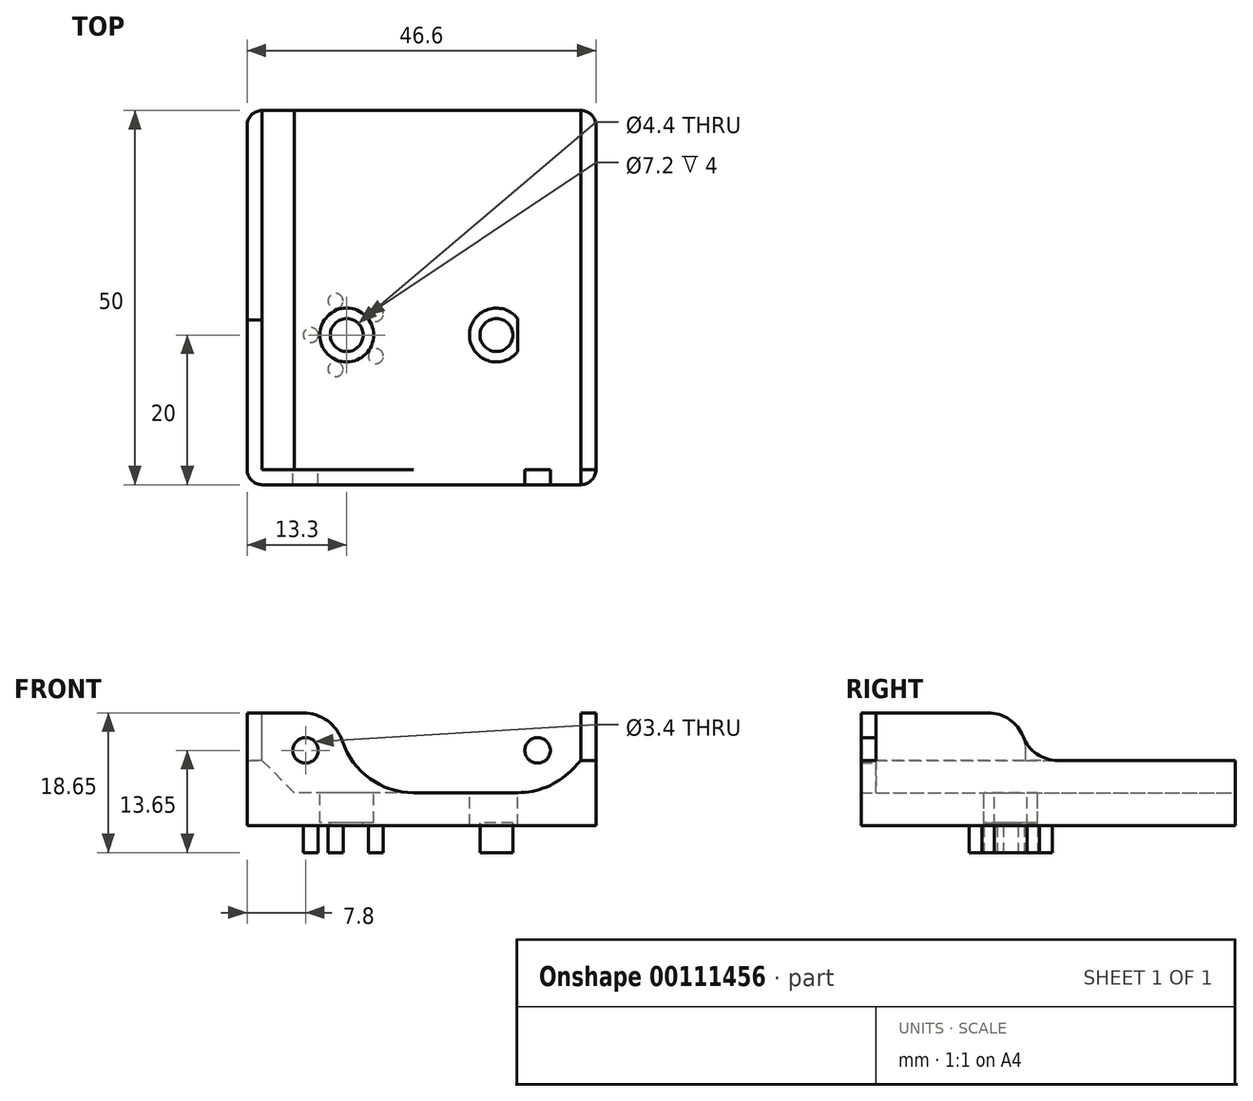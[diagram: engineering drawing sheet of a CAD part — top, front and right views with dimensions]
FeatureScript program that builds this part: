
annotation { "Feature Type Name" : "Feature", "Feature Type Description" : "" }
export const myFeature = defineFeature(function(context is Context, id is Id, definition is map)
    precondition{}
    {
        {
            var Q0;
            Q0=qCreatedBy(makeId("Front.planeOp"),FACE);
            var sketch = newSketch(context, id + "F0", { "sketchPlane" : qUnion([Q0])});
            skLineSegment(sketch, "E0", {"start": v(-23.3, 0) * mm, "end": v(0, 0) * mm});
            skLineSegment(sketch, "E1", {"start": v(0, 8) * mm, "end": v(-17, 8) * mm});
            skLineSegment(sketch, "E2", {"start": v(-17, 8) * mm, "end": v(-21.3, 12.3) * mm});
            skLineSegment(sketch, "E3", {"start": v(0, 0) * mm, "end": v(0, 8) * mm, "construction": true});
            skLineSegment(sketch, "E4", {"start": v(-21.3, 12.3) * mm, "end": v(-23.3, 12.3) * mm});
            skLineSegment(sketch, "E5", {"start": v(-23.3, 12.3) * mm, "end": v(-23.3, 0) * mm});
            skLineSegment(sketch, "E6.MirrorCS", {"start": v(0, 8) * mm, "end": v(17, 8) * mm});
            skLineSegment(sketch, "E7.MirrorCS", {"start": v(17, 8) * mm, "end": v(21.3, 12.3) * mm});
            skLineSegment(sketch, "E8.MirrorCS", {"start": v(21.3, 12.3) * mm, "end": v(23.3, 12.3) * mm});
            skLineSegment(sketch, "E9.MirrorCS", {"start": v(23.3, 12.3) * mm, "end": v(23.3, 0) * mm});
            skLineSegment(sketch, "E10.MirrorCS", {"start": v(23.3, 0) * mm, "end": v(0, 0) * mm});
            skSolve(sketch);
        }
        {
            var Q0;
            Q0=makeQuery(id+"F0.imprint","IMPRINT",FACE,{"disambiguationData":[TD([[makeQuery(id+"F0.imprint","IMPRINT",EDGE,{"derivedFrom":sQuery(id+"F0.wireOp",EDGE,"E0")}),1.0]])]});
            extrude(context, id + "F1", {"entities" : qUnion([Q0]), "endBound" : BoundingType.SYMMETRIC, "depth" : 48 * mm});
        }
        {
            var Q0;
            Q0=makeQuery(id+"F1.opExtrude","CAP_FACE",FACE,{"disambiguationData":[OSD([sQuery(id+"F0.wireOp",EDGE,"E0"),sQuery(id+"F0.wireOp",EDGE,"E1"),sQuery(id+"F0.wireOp",EDGE,"E2"),sQuery(id+"F0.wireOp",EDGE,"E4"),sQuery(id+"F0.wireOp",EDGE,"E5"),sQuery(id+"F0.wireOp",EDGE,"E6.MirrorCS"),sQuery(id+"F0.wireOp",EDGE,"E7.MirrorCS"),sQuery(id+"F0.wireOp",EDGE,"E8.MirrorCS"),sQuery(id+"F0.wireOp",EDGE,"E9.MirrorCS"),sQuery(id+"F0.wireOp",EDGE,"E10.MirrorCS")])],"isStart":false});
            var sketch = newSketch(context, id + "F2", { "sketchPlane" : qUnion([Q0])});
            skLineSegment(sketch, "E11", {"start": v(0, 8) * mm, "end": v(0, 29.15) * mm, "construction": true});
            skCircle(sketch, "E12", {"center": v(-15.5, 13.65) * mm, "radius": 1.7 * mm});
            skCircle(sketch, "E13.MirrorC", {"center": v(15.5, 13.65) * mm, "radius": 1.7 * mm});
            skLineSegment(sketch, "E14", {"start": v(-23.3, 12.3) * mm, "end": v(-23.3, 18.65) * mm});
            skLineSegment(sketch, "E15", {"start": v(-23.3, 18.65) * mm, "end": v(-10.3, 18.65) * mm});
            skLineSegment(sketch, "E16", {"start": v(-10.3, 18.65) * mm, "end": v(-10.3, 8) * mm});
            skLineSegment(sketch, "E17.MirrorCS", {"start": v(23.3, 12.3) * mm, "end": v(23.3, 18.65) * mm});
            skLineSegment(sketch, "E18.MirrorCS", {"start": v(23.3, 18.65) * mm, "end": v(10.3, 18.65) * mm});
            skLineSegment(sketch, "E19.MirrorCS", {"start": v(10.3, 18.65) * mm, "end": v(10.3, 8) * mm});
            skSolve(sketch);
        }
        {
            var Q0;
            Q0=makeQuery(id+"F2.imprint","IMPRINT",FACE,{"disambiguationData":[TD([[makeQuery(id+"F2.imprint","IMPRINT",EDGE,{"derivedFrom":sQuery(id+"F2.wireOp",EDGE,"E12")}),-1.0]])]});
            var Q1;
            Q1=makeQuery(id+"F2.imprint","IMPRINT",FACE,{"disambiguationData":[TD([[makeQuery(id+"F2.imprint","IMPRINT",EDGE,{"derivedFrom":sQuery(id+"F2.wireOp",EDGE,"E13.MirrorC")}),1.0]])]});
            var Q2;
            {var subQ0=makeQuery(id+"F1.opExtrude","CAP_EDGE",EDGE,{"disambiguationData":[OSD([sQuery(id+"F0.wireOp",EDGE,"E2")])],"isStart":false});Q2=makeQuery(id+"F2.imprint","IMPRINT",FACE,{"disambiguationData":[TD([[makeQuery(id+"F2.imprint","IMPRINT",EDGE,{"derivedFrom":subQ0}),1.0]])]});}
            extrude(context, id + "F3", {"entities" : qUnion([Q0, Q1, Q2]), "operationType" : NewBodyOperationType.ADD, "depth" : 2 * mm});
        }
        {
            var Q0;
            Q0=makeQuery(id+"F3.opExtrude","SWEPT_EDGE",EDGE,{"disambiguationData":[OSD([sQuery(id+"F2.wireOp",EDGE,"E15"),sQuery(id+"F2.wireOp",EDGE,"E16")])]});
            var Q1;
            Q1=makeQuery(id+"F3.opExtrude","SWEPT_EDGE",EDGE,{"disambiguationData":[OSD([sQuery(id+"F2.wireOp",EDGE,"E18.MirrorCS"),sQuery(id+"F2.wireOp",EDGE,"E19.MirrorCS")])]});
            fillet(context, id + "F4", {"entities" : qUnion([Q0, Q1]), "radius" : 5.5 * mm, "tangentPropagation" : true, "allowEdgeOverflow" : false});
        }
        {
            var Q0;
            Q0=makeQuery(id+"F3.opExtrude","SWEPT_EDGE",EDGE,{"disambiguationData":[OSD([sQuery(id+"F0.wireOp",EDGE,"E1"),sQuery(id+"F0.wireOp",EDGE,"E6.MirrorCS"),sQuery(id+"F2.wireOp",EDGE,"E16")])]});
            var Q1;
            Q1=makeQuery(id+"F3.opExtrude","SWEPT_EDGE",EDGE,{"disambiguationData":[OSD([sQuery(id+"F0.wireOp",EDGE,"E1"),sQuery(id+"F0.wireOp",EDGE,"E6.MirrorCS"),sQuery(id+"F2.wireOp",EDGE,"E19.MirrorCS")])]});
            fillet(context, id + "F5", {"entities" : qUnion([Q0, Q1]), "radius" : 10 * mm, "tangentPropagation" : true, "allowEdgeOverflow" : false});
        }
        {
            var Q0;
            {var subQ0=sQuery(id+"F2.wireOp",EDGE,"E13.MirrorC");var subQ1=sQuery(id+"F0.wireOp",EDGE,"E9.MirrorCS");var subQ2=sQuery(id+"F0.wireOp",EDGE,"E6.MirrorCS");var subQ3=sQuery(id+"F0.wireOp",EDGE,"E1");var subQ4=sQuery(id+"F2.wireOp",EDGE,"E19.MirrorCS");var subQ5=sQuery(id+"F2.wireOp",EDGE,"E17.MirrorCS");var subQ6=sQuery(id+"F2.wireOp",EDGE,"E18.MirrorCS");Q0=makeQuery(id+"F3.boolean.opBoolean","SPLIT",FACE,{"disambiguationData":[TD([makeQuery(id+"F1.opExtrude","SWEPT_FACE",FACE,{"disambiguationData":[OSD([sQuery(id+"F0.wireOp",EDGE,"E7.MirrorCS")])]})])],"derivedFrom":makeQuery(id+"F3.opExtrude","CAP_FACE",FACE,{"disambiguationData":[OSD([sQuery(id+"F0.wireOp",EDGE,"E0"),subQ3,sQuery(id+"F0.wireOp",EDGE,"E5"),subQ2,subQ1,sQuery(id+"F0.wireOp",EDGE,"E10.MirrorCS"),sQuery(id+"F2.wireOp",EDGE,"E12"),subQ0,sQuery(id+"F2.wireOp",EDGE,"E14"),sQuery(id+"F2.wireOp",EDGE,"E15"),sQuery(id+"F2.wireOp",EDGE,"E16"),subQ5,subQ6,subQ4])],"isStart":true})});}
            var sketch = newSketch(context, id + "F6", { "sketchPlane" : qUnion([Q0])});
            skLineSegment(sketch, "E20.bottom", {"start": v(-21.3, 12.3) * mm, "end": v(-23.3, 12.3) * mm});
            skLineSegment(sketch, "E20.top", {"start": v(-21.3, 18.65) * mm, "end": v(-23.3, 18.65) * mm});
            skLineSegment(sketch, "E20.left", {"start": v(-21.3, 12.3) * mm, "end": v(-21.3, 18.65) * mm});
            skLineSegment(sketch, "E20.right", {"start": v(-23.3, 12.3) * mm, "end": v(-23.3, 18.65) * mm});
            skLineSegment(sketch, "E21", {"start": v(0, 8) * mm, "end": v(0, 18.65) * mm, "construction": true});
            skLineSegment(sketch, "E22.MirrorCS", {"start": v(23.3, 12.3) * mm, "end": v(23.3, 18.65) * mm});
            skLineSegment(sketch, "E23.MirrorCS", {"start": v(21.3, 12.3) * mm, "end": v(21.3, 18.65) * mm});
            skLineSegment(sketch, "E24.MirrorCS", {"start": v(21.3, 18.65) * mm, "end": v(23.3, 18.65) * mm});
            skLineSegment(sketch, "E25.MirrorCS", {"start": v(21.3, 12.3) * mm, "end": v(23.3, 12.3) * mm});
            skSolve(sketch);
        }
        {
            var Q0;
            Q0 = qSketchRegion(id + "F6", true);
            extrude(context, id + "F7", {"entities" : qUnion([Q0]), "operationType" : NewBodyOperationType.ADD, "depth" : 20 * mm});
        }
        {
            var Q0;
            Q0=makeQuery(id+"F7.opExtrude","CAP_EDGE",EDGE,{"disambiguationData":[OSD([sQuery(id+"F6.wireOp",EDGE,"E20.top")])],"isStart":false});
            var Q1;
            Q1=makeQuery(id+"F7.opExtrude","CAP_EDGE",EDGE,{"disambiguationData":[OSD([sQuery(id+"F6.wireOp",EDGE,"E24.MirrorCS")])],"isStart":false});
            fillet(context, id + "F8", {"entities" : qUnion([Q0, Q1]), "radius" : 5 * mm, "tangentPropagation" : true, "allowEdgeOverflow" : false});
        }
        {
            var Q0;
            Q0=makeQuery(id+"F7.opExtrude","CAP_EDGE",EDGE,{"disambiguationData":[OSD([sQuery(id+"F6.wireOp",EDGE,"E25.MirrorCS")])],"isStart":false});
            var Q1;
            Q1=makeQuery(id+"F7.opExtrude","CAP_EDGE",EDGE,{"disambiguationData":[OSD([sQuery(id+"F6.wireOp",EDGE,"E20.bottom")])],"isStart":false});
            fillet(context, id + "F9", {"entities" : qUnion([Q0, Q1]), "radius" : 5 * mm, "tangentPropagation" : true, "allowEdgeOverflow" : false});
        }
        {
            var Q0;
            {var subQ0=sQuery(id+"F0.wireOp",EDGE,"E6.MirrorCS");var subQ1=sQuery(id+"F0.wireOp",EDGE,"E1");Q0=makeQuery(id+"F3.boolean.opBoolean","MERGE",FACE,{"derivedFrom":[makeQuery(id+"F1.opExtrude","SWEPT_FACE",FACE,{"disambiguationData":[OSD([subQ1,subQ0])]}),makeQuery(id+"F3.opExtrude","SWEPT_FACE",FACE,{"disambiguationData":[OSD([subQ1,subQ0])]})]});}
            var sketch = newSketch(context, id + "F10", { "sketchPlane" : qUnion([Q0])});
            skCircle(sketch, "E26", {"center": v(-10, -6) * mm, "radius": 2.2 * mm});
            skLineSegment(sketch, "E27", {"start": v(0, -6) * mm, "end": v(-10, -6) * mm, "construction": true});
            skLineSegment(sketch, "E28", {"start": v(0, -6) * mm, "end": v(0, -12.04) * mm, "construction": true});
            skCircle(sketch, "E29.MirrorC", {"center": v(10, -6) * mm, "radius": 2.2 * mm});
            skCircle(sketch, "E30", {"center": v(-10, -6) * mm, "radius": 3.6 * mm});
            skCircle(sketch, "E31.MirrorC", {"center": v(10, -6) * mm, "radius": 3.6 * mm});
            skSolve(sketch);
        }
        {
            var Q0;
            Q0=makeQuery(id+"F10.imprint","IMPRINT",FACE,{"disambiguationData":[TD([[makeQuery(id+"F10.imprint","IMPRINT",EDGE,{"derivedFrom":sQuery(id+"F10.wireOp",EDGE,"E29.MirrorC")}),-1.0]])]});
            var Q1;
            Q1=makeQuery(id+"F10.imprint","IMPRINT",FACE,{"disambiguationData":[TD([[makeQuery(id+"F10.imprint","IMPRINT",EDGE,{"derivedFrom":sQuery(id+"F10.wireOp",EDGE,"E26")}),1.0]])]});
            extrude(context, id + "F11", {"entities" : qUnion([Q0, Q1]), "operationType" : NewBodyOperationType.REMOVE, "oppositeDirection" : true, "depth" : 8 * mm});
        }
        {
            var Q0;
            Q0=makeQuery(id+"F10.imprint","IMPRINT",FACE,{"disambiguationData":[TD([[makeQuery(id+"F10.imprint","IMPRINT",EDGE,{"derivedFrom":sQuery(id+"F10.wireOp",EDGE,"E29.MirrorC")}),1.0]])]});
            var Q1;
            Q1=makeQuery(id+"F10.imprint","IMPRINT",FACE,{"disambiguationData":[TD([[makeQuery(id+"F10.imprint","IMPRINT",EDGE,{"derivedFrom":sQuery(id+"F10.wireOp",EDGE,"E26")}),-1.0]])]});
            extrude(context, id + "F12", {"entities" : qUnion([Q0, Q1]), "operationType" : NewBodyOperationType.REMOVE, "oppositeDirection" : true, "depth" : 4 * mm});
        }
        {
            var Q0;
            {var subQ0=sQuery(id+"F0.wireOp",EDGE,"E10.MirrorCS");var subQ1=sQuery(id+"F0.wireOp",EDGE,"E0");Q0=makeQuery(id+"F3.boolean.opBoolean","MERGE",FACE,{"derivedFrom":[makeQuery(id+"F1.opExtrude","SWEPT_FACE",FACE,{"disambiguationData":[OSD([subQ1,subQ0])]}),makeQuery(id+"F3.opExtrude","SWEPT_FACE",FACE,{"disambiguationData":[OSD([subQ1,subQ0])]})]});}
            var sketch = newSketch(context, id + "F13", { "sketchPlane" : qUnion([Q0])});
            skLineSegment(sketch, "E32", {"start": v(10, 6) * mm, "end": v(14.8, 6) * mm, "construction": true});
            skCircle(sketch, "E33", {"center": v(14.8, 6) * mm, "radius": 1 * mm});
            skCircle(sketch, "E34.1.0", {"center": v(11.48, 10.57) * mm, "radius": 1 * mm});
            skCircle(sketch, "E34.2.0", {"center": v(6.12, 8.82) * mm, "radius": 1 * mm});
            skCircle(sketch, "E34.3.0", {"center": v(6.12, 3.18) * mm, "radius": 1 * mm});
            skPoint(sketch, "E34.center", {"position": v(10, 6) * mm});
            skCircle(sketch, "E35.1.4.0", {"center": v(11.48, 1.43) * mm, "radius": 1 * mm});
            skLineSegment(sketch, "E36", {"start": v(0, 26) * mm, "end": v(0, -24) * mm, "construction": true});
            skCircle(sketch, "E37.MirrorC", {"center": v(-6.12, 8.82) * mm, "radius": 1 * mm});
            skCircle(sketch, "E38.MirrorC", {"center": v(-11.48, 10.57) * mm, "radius": 1 * mm});
            skCircle(sketch, "E39.MirrorC", {"center": v(-6.12, 3.18) * mm, "radius": 1 * mm});
            skCircle(sketch, "E40.MirrorC", {"center": v(-11.48, 1.43) * mm, "radius": 1 * mm});
            skCircle(sketch, "E41.MirrorC", {"center": v(-14.8, 6) * mm, "radius": 1 * mm});
            skSolve(sketch);
        }
        {
            var Q0;
            Q0=makeQuery(id+"F13.imprint","IMPRINT",FACE,{"disambiguationData":[TD([[makeQuery(id+"F13.imprint","IMPRINT",EDGE,{"derivedFrom":sQuery(id+"F13.wireOp",EDGE,"E34.3.0")}),1.0]])]});
            var Q1;
            Q1=makeQuery(id+"F13.imprint","IMPRINT",FACE,{"disambiguationData":[TD([[makeQuery(id+"F13.imprint","IMPRINT",EDGE,{"derivedFrom":sQuery(id+"F13.wireOp",EDGE,"E34.2.0")}),1.0]])]});
            var Q2;
            Q2=makeQuery(id+"F13.imprint","IMPRINT",FACE,{"disambiguationData":[TD([[makeQuery(id+"F13.imprint","IMPRINT",EDGE,{"derivedFrom":sQuery(id+"F13.wireOp",EDGE,"E34.1.0")}),1.0]])]});
            var Q3;
            Q3=makeQuery(id+"F13.imprint","IMPRINT",FACE,{"disambiguationData":[TD([[makeQuery(id+"F13.imprint","IMPRINT",EDGE,{"derivedFrom":sQuery(id+"F13.wireOp",EDGE,"E35.1.4.0")}),1.0]])]});
            var Q4;
            Q4=makeQuery(id+"F13.imprint","IMPRINT",FACE,{"disambiguationData":[TD([[makeQuery(id+"F13.imprint","IMPRINT",EDGE,{"derivedFrom":sQuery(id+"F13.wireOp",EDGE,"E33")}),1.0]])]});
            var Q5;
            Q5=makeQuery(id+"F13.imprint","IMPRINT",FACE,{"disambiguationData":[TD([[makeQuery(id+"F13.imprint","IMPRINT",EDGE,{"derivedFrom":sQuery(id+"F13.wireOp",EDGE,"E38.MirrorC")}),-1.0]])]});
            var Q6;
            Q6=makeQuery(id+"F13.imprint","IMPRINT",FACE,{"disambiguationData":[TD([[makeQuery(id+"F13.imprint","IMPRINT",EDGE,{"derivedFrom":sQuery(id+"F13.wireOp",EDGE,"E41.MirrorC")}),-1.0]])]});
            var Q7;
            Q7=makeQuery(id+"F13.imprint","IMPRINT",FACE,{"disambiguationData":[TD([[makeQuery(id+"F13.imprint","IMPRINT",EDGE,{"derivedFrom":sQuery(id+"F13.wireOp",EDGE,"E40.MirrorC")}),-1.0]])]});
            var Q8;
            Q8=makeQuery(id+"F13.imprint","IMPRINT",FACE,{"disambiguationData":[TD([[makeQuery(id+"F13.imprint","IMPRINT",EDGE,{"derivedFrom":sQuery(id+"F13.wireOp",EDGE,"E39.MirrorC")}),-1.0]])]});
            var Q9;
            Q9=makeQuery(id+"F13.imprint","IMPRINT",FACE,{"disambiguationData":[TD([[makeQuery(id+"F13.imprint","IMPRINT",EDGE,{"derivedFrom":sQuery(id+"F13.wireOp",EDGE,"E37.MirrorC")}),-1.0]])]});
            extrude(context, id + "F14", {"entities" : qUnion([Q0, Q1, Q2, Q3, Q4, Q5, Q6, Q7, Q8, Q9]), "operationType" : NewBodyOperationType.REMOVE, "oppositeDirection" : true, "depth" : 3.6 * mm});
        }
        {
            var Q0;
            Q0=makeQuery(id+"F1.opExtrude","CAP_EDGE",EDGE,{"disambiguationData":[OSD([sQuery(id+"F0.wireOp",EDGE,"E5")])],"isStart":true});
            var Q1;
            Q1=makeQuery(id+"F1.opExtrude","CAP_EDGE",EDGE,{"disambiguationData":[OSD([sQuery(id+"F0.wireOp",EDGE,"E9.MirrorCS")])],"isStart":true});
            var Q2;
            Q2=makeQuery(id+"F3.opExtrude","CAP_EDGE",EDGE,{"disambiguationData":[OSD([sQuery(id+"F0.wireOp",EDGE,"E5"),sQuery(id+"F2.wireOp",EDGE,"E14")])],"isStart":false});
            var Q3;
            Q3=makeQuery(id+"F3.opExtrude","CAP_EDGE",EDGE,{"disambiguationData":[OSD([sQuery(id+"F0.wireOp",EDGE,"E9.MirrorCS"),sQuery(id+"F2.wireOp",EDGE,"E17.MirrorCS")])],"isStart":false});
            fillet(context, id + "F15", {"entities" : qUnion([Q0, Q1, Q2, Q3]), "radius" : 2 * mm, "tangentPropagation" : true, "allowEdgeOverflow" : false});
        }
    });
